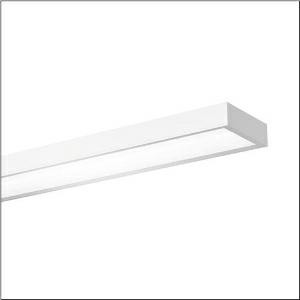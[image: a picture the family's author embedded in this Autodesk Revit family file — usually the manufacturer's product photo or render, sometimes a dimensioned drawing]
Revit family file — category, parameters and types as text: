
# Revit family: sport_31_51hs12dc4eca
name_source: partatom
category: Lighting Fixtures
units: mm (PartAtom-declared; Revit-internal decimal feet)

## family parameters
Cut with Voids When Loaded = No
Host = Face
Light Source = No
Part Type = Normal
Room Calculation Point = No
Round Connector Dimension = Use Diameter
Shared = No

## types (1)
- --- (1 x LED, 11990 lm, 89.4 W, 4000K)
    Apparent Load = 89 VA
    CIE Flux Codes = 65 89 97 100 100
    Color Rendering = 80
    Color Temperature = 4000K
    Default Elevation = 1800 mm
    Description = Sport 31, high bay luminaire, primary light control with reflector, of sheet steel, primary anti-glare with prismatic structure, of PC, primary optical cover: cover panel, of PC, light emission: direct distribution, primary light characteristic: symmetric, installation type: suspended mounting, recessed, surface-mounted, LED, rated luminous flux: 12.000lm, luminous efficacy: 137lm/W, light colour: 840, colour temperature: 4000K, control gear: DALI 2, with terminal, 5-pole, max. 2.5mm², mains connection: 220..240V, AC/DC, 50/60Hz, rated input power: 88W, housing, of sheet steel, traffic white (RAL 9016), length: 1.540mm, width: 315mm, height: 95mm, protection rating (complete): IP20, protection rating (lamp compartment, on room side): IP50, insulation class (complete): insulation class I (protective earthing), certification: CE, ENEC, UKCA, ball protection: ball impact resistant with ceiling mounting or chain suspension, impact resistance: IK08, permissible operating ambient temperature: -20..+35°C, standard: DIN 18032-3, EN 60598-2-22, packaging unit: 1 piece
    Height = 100 mm  [stored 0.328084 ft]
    Lamp = 1 x LED
    Lamp Light Flux = 11990 lm
    Lamp Power = 89.4 W
    Lamp count = 1
    Length = 1500 mm
    Luminous efficacy = 134 lm/W
    Manufacturer = Siteco
    ModVariant = No
    Model = 51HS12DC4ECA
    Mounting Place = Ceiling
    Mounting Type = Pendant
    Number of Poles = 1
    OnlyDefault = Yes
    Power Factor = 1
    Product Name = Sport 31
    Product group = high bay luminaire
    ProductGroupID = 901
    Protection Class = Protection class I
    Protection Degree = IP 20
    RLX_Detail_Level = 1
    RLX_Emergency_Light_Flux = 0 lm
    RLX_Emergency_Type = 0
    RLX_Emergency_Type_DB = No
    RlxData = <blob elided: 22809 chars, md5=ffbe4a27>
    Socket = socket
    Standby Power = 0 W
    System Light Flux = 11990 lm
    System Power = 89 W
    Type Comments = factory setting: luminous flux: 100 % | dim-lin: 254 | 380 mA
    Type Image = l_1006823.jpg
    URL = http://relux.com
    VarID = @adj_218479
    Voltage = 0 V
    Weight = 0.00 kg
    Width = 315 mm

note: [stored X ft] marks values corroborated as IEEE doubles in the binary element streams (Revit-internal decimal feet)

## geometry (parser evidence)
native form markers: Blend x4, Sweep x12
no freeform markers — native parametric forms only
